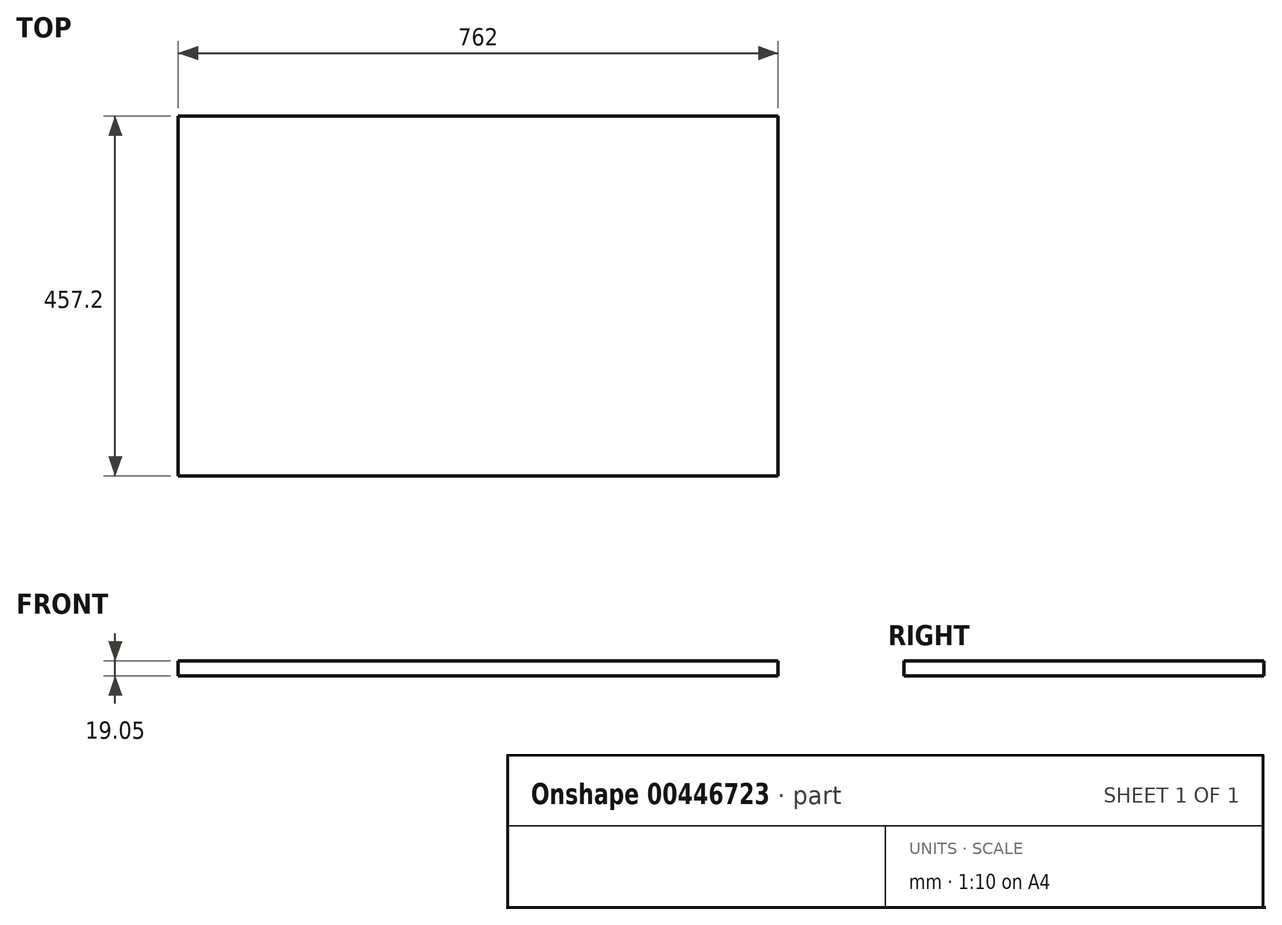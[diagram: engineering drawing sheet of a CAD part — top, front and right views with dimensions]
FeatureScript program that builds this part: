
annotation { "Feature Type Name" : "Feature", "Feature Type Description" : "" }
export const myFeature = defineFeature(function(context is Context, id is Id, definition is map)
    precondition{}
    {
        {
            var Q0;
            Q0=qCreatedBy(makeId("Top.planeOp"),FACE);
            var sketch = newSketch(context, id + "F0", { "sketchPlane" : qUnion([Q0])});
            skLineSegment(sketch, "E0.bottom", {"start": v(-386.8, 127.75) * mm, "end": v(375.2, 127.75) * mm});
            skLineSegment(sketch, "E0.top", {"start": v(-386.8, -329.45) * mm, "end": v(375.2, -329.45) * mm});
            skLineSegment(sketch, "E0.left", {"start": v(-386.8, 127.75) * mm, "end": v(-386.8, -329.45) * mm});
            skLineSegment(sketch, "E0.right", {"start": v(375.2, 127.75) * mm, "end": v(375.2, -329.45) * mm});
            skSolve(sketch);
        }
        {
            var Q0;
            Q0 = qSketchRegion(id + "F0", true);
            var Q1;
            Q1=makeQuery(id+"F0.imprint","IMPRINT",FACE,{"disambiguationData":[TD([[makeQuery(id+"F0.imprint","IMPRINT",EDGE,{"derivedFrom":sQuery(id+"F0.wireOp",EDGE,"E0.bottom")}),-1.0]])]});
            extrude(context, id + "F1", {"entities" : qUnion([Q0, Q1]), "depth" : 19.05 * mm});
        }
    });
